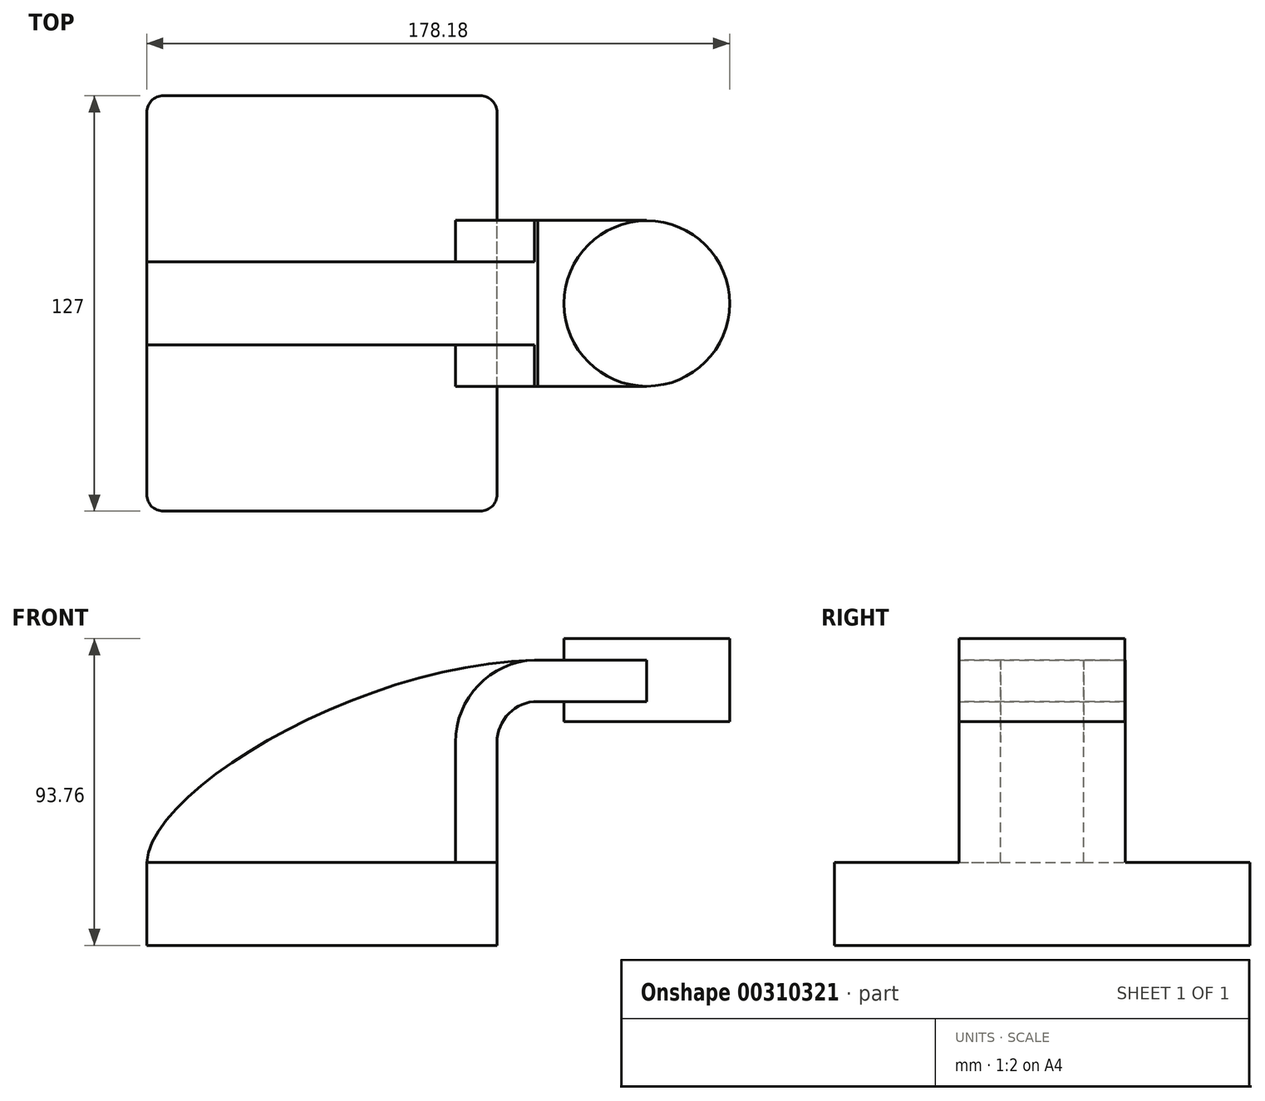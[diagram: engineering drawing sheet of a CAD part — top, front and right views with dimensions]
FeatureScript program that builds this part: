
annotation { "Feature Type Name" : "Feature", "Feature Type Description" : "" }
export const myFeature = defineFeature(function(context is Context, id is Id, definition is map)
    precondition{}
    {
        {
            var Q0;
            Q0=qCreatedBy(makeId("Front.planeOp"),FACE);
            var sketch = newSketch(context, id + "F0", { "sketchPlane" : qUnion([Q0])});
            skLineSegment(sketch, "E0.bottom", {"start": v(53.53, -12.7) * mm, "end": v(-53.53, -12.7) * mm});
            skLineSegment(sketch, "E0.top", {"start": v(53.53, 12.7) * mm, "end": v(-53.53, 12.7) * mm});
            skLineSegment(sketch, "E0.left", {"start": v(53.53, -12.7) * mm, "end": v(53.53, 12.7) * mm});
            skLineSegment(sketch, "E0.right", {"start": v(-53.53, -12.7) * mm, "end": v(-53.53, 12.7) * mm});
            skPoint(sketch, "E0.middle", {"position": v(0, 0) * mm});
            skLineSegment(sketch, "E1.bottom", {"start": v(124.65, 55.66) * mm, "end": v(73.85, 55.66) * mm});
            skLineSegment(sketch, "E1.top", {"start": v(124.65, 81.06) * mm, "end": v(73.85, 81.06) * mm});
            skLineSegment(sketch, "E1.left", {"start": v(124.65, 55.66) * mm, "end": v(124.65, 81.06) * mm});
            skLineSegment(sketch, "E1.right", {"start": v(73.85, 55.66) * mm, "end": v(73.85, 81.06) * mm});
            skPoint(sketch, "E1.middle", {"position": v(99.25, 68.36) * mm});
            skLineSegment(sketch, "E2", {"start": v(53.53, 12.7) * mm, "end": v(53.53, 49.38) * mm});
            skLineSegment(sketch, "E3", {"start": v(66.02, 61.86) * mm, "end": v(99.34, 61.86) * mm});
            skArc(sketch, "E4", {"start": v(53.53, 49.38) * mm, "mid": v(57.19, 58.2) * mm, "end": v(66.02, 61.86) * mm});
            skLineSegment(sketch, "E5.0", {"start": v(66.02, 74.56) * mm, "end": v(99.34, 74.56) * mm});
            skArc(sketch, "E5.1", {"start": v(40.83, 49.38) * mm, "mid": v(48.2, 67.19) * mm, "end": v(66.02, 74.56) * mm});
            skLineSegment(sketch, "E5.2", {"start": v(40.83, 12.7) * mm, "end": v(40.83, 49.38) * mm});
            skFitSpline(sketch, "E6", {"points": [v(-53.53, 12.7) * mm, v(66.02, 74.56) * mm], "startDerivative": vector(3.84, 68.33) * mm, "endDerivative": vector(158.78, 2.6) * mm});
            skLineSegment(sketch, "E7", {"start": v(99.34, 81.06) * mm, "end": v(99.34, 74.56) * mm});
            skLineSegment(sketch, "E8", {"start": v(99.34, 74.56) * mm, "end": v(99.34, 61.86) * mm});
            skLineSegment(sketch, "E9", {"start": v(99.34, 61.86) * mm, "end": v(99.34, 55.66) * mm});
            skSolve(sketch);
        }
        {
            var Q0;
            Q0=makeQuery(id+"F0.imprint","IMPRINT",FACE,{"disambiguationData":[TD([[makeQuery(id+"F0.imprint","IMPRINT",EDGE,{"derivedFrom":sQuery(id+"F0.wireOp",EDGE,"E0.bottom")}),-1.0]])]});
            extrude(context, id + "F1", {"entities" : qUnion([Q0]), "endBound" : BoundingType.SYMMETRIC, "depth" : 127 * mm});
        }
        {
            var Q0;
            {var subQ4=sQuery(id+"F0.wireOp",EDGE,"E2");Q0=makeQuery(id+"F0.imprint","IMPRINT",FACE,{"disambiguationData":[TD([[makeQuery(id+"F0.imprint","IMPRINT",EDGE,{"derivedFrom":subQ4}),1.0]])]});}
            var Q1;
            {var subQ5=sQuery(id+"F0.wireOp",EDGE,"E8");Q1=makeQuery(id+"F0.imprint","IMPRINT",FACE,{"disambiguationData":[TD([[makeQuery(id+"F0.imprint","IMPRINT",EDGE,{"derivedFrom":subQ5}),-1.0]])]});}
            extrude(context, id + "F2", {"entities" : qUnion([Q0, Q1]), "operationType" : NewBodyOperationType.ADD, "endBound" : BoundingType.SYMMETRIC, "depth" : 50.8 * mm});
        }
        {
            var Q0;
            {var subQ3=sQuery(id+"F0.wireOp",EDGE,"E5.2");Q0=makeQuery(id+"F0.imprint","IMPRINT",FACE,{"disambiguationData":[TD([[makeQuery(id+"F0.imprint","IMPRINT",EDGE,{"derivedFrom":subQ3}),1.0]])]});}
            extrude(context, id + "F3", {"entities" : qUnion([Q0]), "operationType" : NewBodyOperationType.ADD, "endBound" : BoundingType.SYMMETRIC, "depth" : 25.4 * mm});
        }
        {
            var Q0;
            {var subQ1=sQuery(id+"F0.wireOp",EDGE,"E1.left");Q0=makeQuery(id+"F0.imprint","IMPRINT",FACE,{"disambiguationData":[TD([[makeQuery(id+"F0.imprint","IMPRINT",EDGE,{"derivedFrom":subQ1}),1.0]])]});}
            var Q1;
            Q1=sQuery(id+"F0.wireOp",EDGE,"E9");
            revolve(context, id + "F4", {"operationType" : NewBodyOperationType.ADD, "entities" : qUnion([Q0]), "axis" : qUnion([Q1]), "revolveType" : RevolveType.FULL});
        }
        {
            var Q0;
            Q0=makeQuery(id+"F1.opExtrude","CAP_EDGE",EDGE,{"disambiguationData":[OSD([sQuery(id+"F0.wireOp",EDGE,"E0.right")])],"isStart":false});
            var Q1;
            Q1=makeQuery(id+"F1.opExtrude","CAP_EDGE",EDGE,{"disambiguationData":[OSD([sQuery(id+"F0.wireOp",EDGE,"E0.right")])],"isStart":true});
            var Q2;
            Q2=makeQuery(id+"F1.opExtrude","CAP_EDGE",EDGE,{"disambiguationData":[OSD([sQuery(id+"F0.wireOp",EDGE,"E0.left")])],"isStart":true});
            var Q3;
            Q3=makeQuery(id+"F1.opExtrude","CAP_EDGE",EDGE,{"disambiguationData":[OSD([sQuery(id+"F0.wireOp",EDGE,"E0.left")])],"isStart":false});
            fillet(context, id + "F5", {"entities" : qUnion([Q0, Q1, Q2, Q3]), "radius" : 5.08 * mm, "tangentPropagation" : true, "allowEdgeOverflow" : false});
        }
    });
